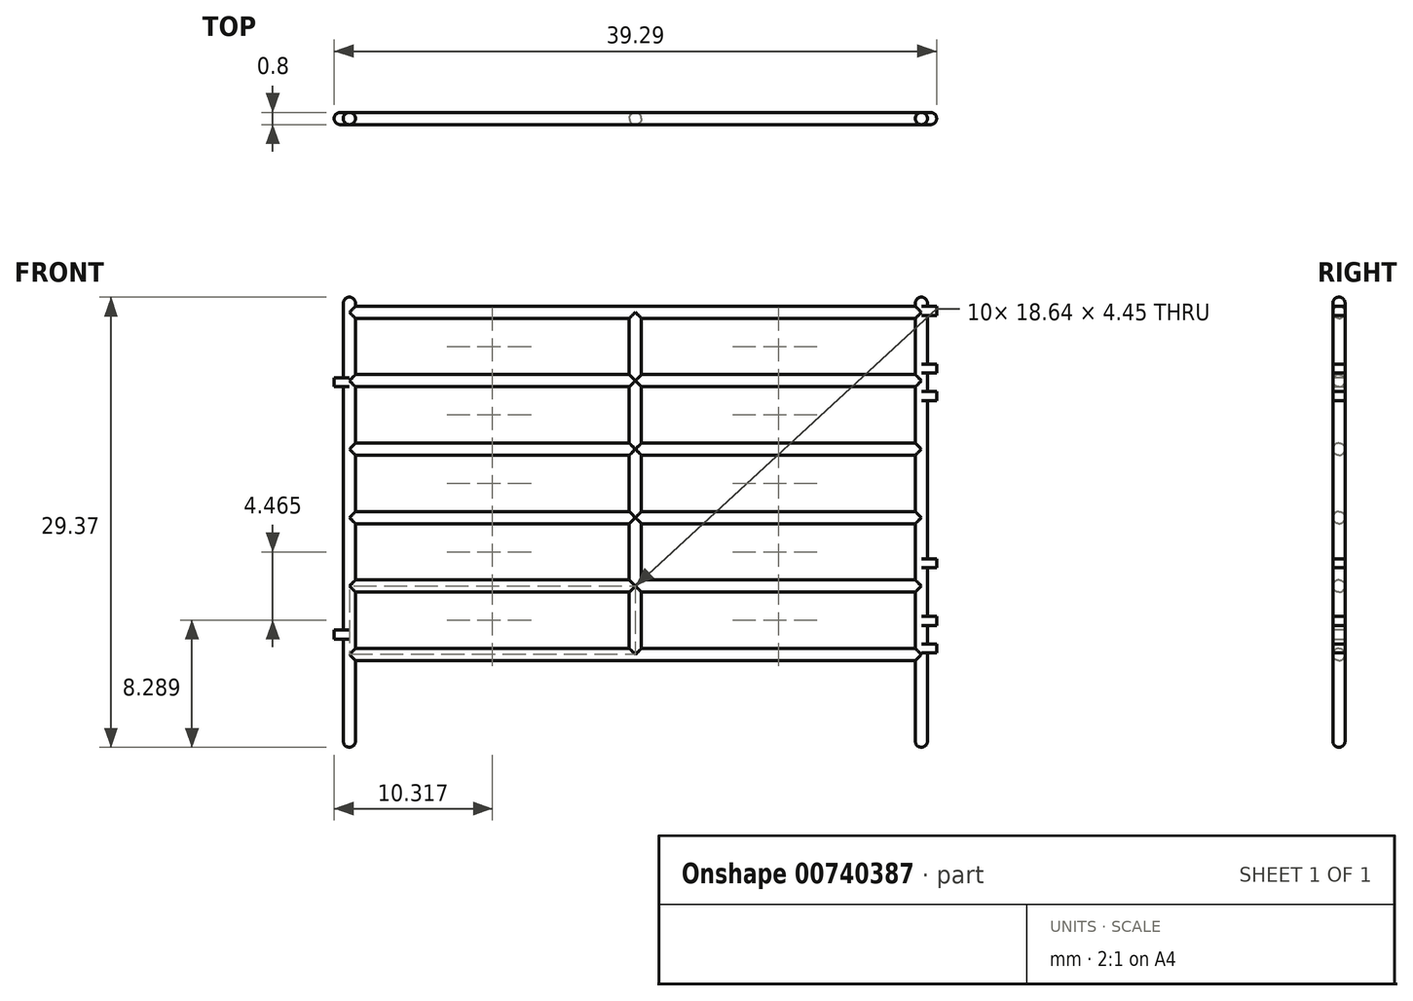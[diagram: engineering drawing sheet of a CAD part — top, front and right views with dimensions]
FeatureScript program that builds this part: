
annotation { "Feature Type Name" : "Feature", "Feature Type Description" : "" }
export const myFeature = defineFeature(function(context is Context, id is Id, definition is map)
    precondition{}
    {
        {
            var Q0;
            Q0=qCreatedBy(makeId("Front.planeOp"),FACE);
            var sketch = newSketch(context, id + "F0", { "sketchPlane" : qUnion([Q0])});
            skLineSegment(sketch, "E0", {"start": v(0, 0) * mm, "end": v(-36.51, 0) * mm});
            skLineSegment(sketch, "E1.0", {"start": v(0, 0.8) * mm, "end": v(-17.86, 0.8) * mm});
            skLineSegment(sketch, "E2.0", {"start": v(0, 4.46) * mm, "end": v(-17.86, 4.46) * mm});
            skLineSegment(sketch, "E3.0", {"start": v(0, 5.26) * mm, "end": v(-17.86, 5.26) * mm});
            skLineSegment(sketch, "E4.0", {"start": v(0, 8.93) * mm, "end": v(-17.86, 8.93) * mm});
            skLineSegment(sketch, "E5.0", {"start": v(0, 9.72) * mm, "end": v(-17.86, 9.72) * mm});
            skLineSegment(sketch, "E6.0", {"start": v(0, 13.4) * mm, "end": v(-17.86, 13.4) * mm});
            skLineSegment(sketch, "E7.0", {"start": v(0, 14.19) * mm, "end": v(-17.86, 14.19) * mm});
            skLineSegment(sketch, "E8.0", {"start": v(0, 17.86) * mm, "end": v(-17.86, 17.86) * mm});
            skLineSegment(sketch, "E9.0", {"start": v(0, 18.65) * mm, "end": v(-17.86, 18.65) * mm});
            skLineSegment(sketch, "E10.0", {"start": v(0, 22.32) * mm, "end": v(-17.86, 22.32) * mm});
            skLineSegment(sketch, "E11.0", {"start": v(0, 23.12) * mm, "end": v(-36.51, 23.12) * mm});
            skLineSegment(sketch, "E12", {"start": v(-36.51, 23.12) * mm, "end": v(-36.51, 23.32) * mm});
            skLineSegment(sketch, "E13", {"start": v(0, 23.12) * mm, "end": v(0, 23.32) * mm});
            skPoint(sketch, "E14", {"position": v(-37.3, 23.32) * mm});
            skLineSegment(sketch, "E15", {"start": v(-37.3, 23.32) * mm, "end": v(-37.3, 18.45) * mm});
            skLineSegment(sketch, "E16", {"start": v(-36.51, -5.26) * mm, "end": v(-36.51, 0) * mm});
            skLineSegment(sketch, "E17", {"start": v(-36.51, 0.8) * mm, "end": v(-36.51, 4.46) * mm});
            skLineSegment(sketch, "E18", {"start": v(-36.51, 5.26) * mm, "end": v(-36.51, 8.93) * mm});
            skLineSegment(sketch, "E19", {"start": v(-36.51, 9.72) * mm, "end": v(-36.51, 13.4) * mm});
            skLineSegment(sketch, "E20", {"start": v(-36.51, 14.19) * mm, "end": v(-36.51, 17.86) * mm});
            skLineSegment(sketch, "E21", {"start": v(-36.51, 18.65) * mm, "end": v(-36.51, 22.32) * mm});
            skLineSegment(sketch, "E22", {"start": v(0.8, 23.32) * mm, "end": v(0.8, 23.12) * mm});
            skLineSegment(sketch, "E23", {"start": v(0, -5.26) * mm, "end": v(0, 0) * mm});
            skLineSegment(sketch, "E24", {"start": v(0, 0.8) * mm, "end": v(0, 4.46) * mm});
            skLineSegment(sketch, "E25", {"start": v(0, 5.26) * mm, "end": v(0, 8.93) * mm});
            skLineSegment(sketch, "E26", {"start": v(0, 9.72) * mm, "end": v(0, 13.4) * mm});
            skLineSegment(sketch, "E27", {"start": v(0, 14.19) * mm, "end": v(0, 17.86) * mm});
            skLineSegment(sketch, "E28", {"start": v(0, 18.65) * mm, "end": v(0, 22.32) * mm});
            skArc(sketch, "E29", {"start": v(-37.3, -5.26) * mm, "mid": v(-36.9, -5.66) * mm, "end": v(-36.51, -5.26) * mm});
            skArc(sketch, "E30", {"start": v(0.8, -5.26) * mm, "mid": v(0.4, -5.66) * mm, "end": v(0, -5.26) * mm});
            skArc(sketch, "E31", {"start": v(0.8, 23.32) * mm, "mid": v(0.4, 23.71) * mm, "end": v(0, 23.32) * mm});
            skArc(sketch, "E32", {"start": v(-37.3, 23.32) * mm, "mid": v(-36.9, 23.71) * mm, "end": v(-36.51, 23.32) * mm});
            skPoint(sketch, "E33", {"position": v(0.8, 0.5) * mm});
            skLineSegment(sketch, "E34", {"start": v(0.8, 0.5) * mm, "end": v(1.39, 0.5) * mm});
            skLineSegment(sketch, "E35", {"start": v(1.39, 0.5) * mm, "end": v(1.39, 1.1) * mm});
            skLineSegment(sketch, "E36", {"start": v(1.39, 1.1) * mm, "end": v(0.8, 1.1) * mm});
            skLineSegment(sketch, "E37", {"start": v(0.8, 2.28) * mm, "end": v(1.39, 2.28) * mm});
            skLineSegment(sketch, "E38", {"start": v(1.39, 2.28) * mm, "end": v(1.39, 2.88) * mm});
            skLineSegment(sketch, "E39", {"start": v(1.39, 2.88) * mm, "end": v(0.8, 2.88) * mm});
            skLineSegment(sketch, "E40", {"start": v(0.8, 6.05) * mm, "end": v(1.39, 6.05) * mm});
            skLineSegment(sketch, "E41", {"start": v(1.39, 6.05) * mm, "end": v(1.39, 6.65) * mm});
            skLineSegment(sketch, "E42", {"start": v(1.39, 6.65) * mm, "end": v(0.8, 6.65) * mm});
            skLineSegment(sketch, "E43", {"start": v(0.8, 16.97) * mm, "end": v(1.39, 16.97) * mm});
            skLineSegment(sketch, "E44", {"start": v(1.39, 16.97) * mm, "end": v(1.39, 17.56) * mm});
            skLineSegment(sketch, "E45", {"start": v(1.39, 17.56) * mm, "end": v(0.8, 17.56) * mm});
            skLineSegment(sketch, "E46", {"start": v(0.8, 18.75) * mm, "end": v(1.39, 18.75) * mm});
            skLineSegment(sketch, "E47", {"start": v(1.39, 18.75) * mm, "end": v(1.39, 19.35) * mm});
            skLineSegment(sketch, "E48", {"start": v(1.39, 19.35) * mm, "end": v(0.8, 19.35) * mm});
            skLineSegment(sketch, "E49", {"start": v(0.8, 22.52) * mm, "end": v(1.39, 22.52) * mm});
            skLineSegment(sketch, "E50", {"start": v(1.39, 22.52) * mm, "end": v(1.39, 23.12) * mm});
            skLineSegment(sketch, "E51", {"start": v(1.39, 23.12) * mm, "end": v(0.8, 23.12) * mm});
            skPoint(sketch, "E52", {"position": v(-37.3, 1.39) * mm});
            skPoint(sketch, "E53", {"position": v(-37.9, 1.39) * mm});
            skLineSegment(sketch, "E54", {"start": v(-37.3, 1.39) * mm, "end": v(-37.9, 1.39) * mm});
            skLineSegment(sketch, "E55", {"start": v(-37.9, 1.39) * mm, "end": v(-37.9, 1.98) * mm});
            skLineSegment(sketch, "E56", {"start": v(-37.9, 1.98) * mm, "end": v(-37.3, 1.98) * mm});
            skPoint(sketch, "E57", {"position": v(-37.3, 17.86) * mm});
            skLineSegment(sketch, "E58", {"start": v(-37.3, 17.86) * mm, "end": v(-37.9, 17.86) * mm});
            skLineSegment(sketch, "E59", {"start": v(-37.9, 17.86) * mm, "end": v(-37.9, 18.45) * mm});
            skLineSegment(sketch, "E60", {"start": v(-37.9, 18.45) * mm, "end": v(-37.3, 18.45) * mm});
            skLineSegment(sketch, "E61.trimOffspring", {"start": v(-37.3, 17.86) * mm, "end": v(-37.3, 1.98) * mm});
            skLineSegment(sketch, "E62.trimOffspring", {"start": v(-37.3, 1.39) * mm, "end": v(-37.3, -5.26) * mm});
            skLineSegment(sketch, "E63.trimOffspring", {"start": v(0.8, 0.5) * mm, "end": v(0.8, -5.26) * mm});
            skLineSegment(sketch, "E64.trimOffspring", {"start": v(0.8, 2.28) * mm, "end": v(0.8, 1.1) * mm});
            skLineSegment(sketch, "E65.trimOffspring", {"start": v(0.8, 6.05) * mm, "end": v(0.8, 2.88) * mm});
            skLineSegment(sketch, "E66.trimOffspring", {"start": v(0.8, 16.97) * mm, "end": v(0.8, 6.65) * mm});
            skLineSegment(sketch, "E67.trimOffspring", {"start": v(0.8, 18.75) * mm, "end": v(0.8, 17.56) * mm});
            skLineSegment(sketch, "E68.trimOffspring", {"start": v(0.8, 22.52) * mm, "end": v(0.8, 19.35) * mm});
            skLineSegment(sketch, "E69", {"start": v(-18.65, 0.8) * mm, "end": v(-18.65, 4.46) * mm});
            skLineSegment(sketch, "E70.0", {"start": v(-17.86, 0.8) * mm, "end": v(-17.86, 4.46) * mm});
            skLineSegment(sketch, "E71", {"start": v(-18.65, 5.26) * mm, "end": v(-18.65, 8.93) * mm});
            skLineSegment(sketch, "E72", {"start": v(-17.86, 5.26) * mm, "end": v(-17.86, 8.93) * mm});
            skLineSegment(sketch, "E73", {"start": v(-18.65, 9.72) * mm, "end": v(-18.65, 13.4) * mm});
            skLineSegment(sketch, "E74", {"start": v(-17.86, 9.72) * mm, "end": v(-17.86, 13.4) * mm});
            skPoint(sketch, "E74.endSnap0", {"position": v(-18.26, 13.4) * mm});
            skLineSegment(sketch, "E75", {"start": v(-18.65, 14.19) * mm, "end": v(-18.65, 17.86) * mm});
            skLineSegment(sketch, "E76", {"start": v(-17.86, 14.19) * mm, "end": v(-17.86, 17.86) * mm});
            skLineSegment(sketch, "E77", {"start": v(-18.65, 18.65) * mm, "end": v(-18.65, 22.32) * mm});
            skLineSegment(sketch, "E78", {"start": v(-17.86, 18.65) * mm, "end": v(-17.86, 22.32) * mm});
            skLineSegment(sketch, "E79.trimOffspring", {"start": v(-18.65, 22.32) * mm, "end": v(-36.51, 22.32) * mm});
            skLineSegment(sketch, "E80.trimOffspring", {"start": v(-18.65, 18.65) * mm, "end": v(-36.51, 18.65) * mm});
            skLineSegment(sketch, "E81.trimOffspring", {"start": v(-18.65, 17.86) * mm, "end": v(-36.51, 17.86) * mm});
            skLineSegment(sketch, "E82.trimOffspring", {"start": v(-18.65, 14.19) * mm, "end": v(-36.51, 14.19) * mm});
            skLineSegment(sketch, "E83.trimOffspring", {"start": v(-18.65, 13.4) * mm, "end": v(-36.51, 13.4) * mm});
            skLineSegment(sketch, "E84.trimOffspring", {"start": v(-18.65, 9.72) * mm, "end": v(-36.51, 9.72) * mm});
            skLineSegment(sketch, "E85.trimOffspring", {"start": v(-18.65, 8.93) * mm, "end": v(-36.51, 8.93) * mm});
            skLineSegment(sketch, "E86.trimOffspring", {"start": v(-18.65, 5.26) * mm, "end": v(-36.51, 5.26) * mm});
            skLineSegment(sketch, "E87.trimOffspring", {"start": v(-18.65, 4.46) * mm, "end": v(-36.51, 4.46) * mm});
            skLineSegment(sketch, "E88.trimOffspring", {"start": v(-18.65, 0.8) * mm, "end": v(-36.51, 0.8) * mm});
            skSolve(sketch);
        }
        {
            var Q0;
            Q0=makeQuery(id+"F0.imprint","IMPRINT",FACE,{"disambiguationData":[TD([[makeQuery(id+"F0.imprint","IMPRINT",EDGE,{"derivedFrom":sQuery(id+"F0.wireOp",EDGE,"E0")}),-1.0]])]});
            extrude(context, id + "F1", {"entities" : qUnion([Q0]), "endBound" : BoundingType.SYMMETRIC, "depth" : 0.8 * mm, "offsetDistance" : 25.4 * mm});
        }
        {
            var Q0;
            Q0=makeQuery(id+"F1.opExtrude","CAP_EDGE",EDGE,{"disambiguationData":[OSD([sQuery(id+"F0.wireOp",EDGE,"E79.trimOffspring")])],"isStart":false});
            var Q1;
            Q1=makeQuery(id+"F1.opExtrude","CAP_EDGE",EDGE,{"disambiguationData":[OSD([sQuery(id+"F0.wireOp",EDGE,"E11.0")])],"isStart":false});
            var Q2;
            Q2=makeQuery(id+"F1.opExtrude","CAP_EDGE",EDGE,{"disambiguationData":[OSD([sQuery(id+"F0.wireOp",EDGE,"E32")])],"isStart":false});
            var Q3;
            Q3=makeQuery(id+"F1.opExtrude","CAP_EDGE",EDGE,{"disambiguationData":[OSD([sQuery(id+"F0.wireOp",EDGE,"E12")])],"isStart":false});
            var Q4;
            Q4=makeQuery(id+"F1.opExtrude","CAP_EDGE",EDGE,{"disambiguationData":[OSD([sQuery(id+"F0.wireOp",EDGE,"E15")])],"isStart":false});
            var Q5;
            Q5=makeQuery(id+"F1.opExtrude","CAP_EDGE",EDGE,{"disambiguationData":[OSD([sQuery(id+"F0.wireOp",EDGE,"E21")])],"isStart":false});
            var Q6;
            Q6=makeQuery(id+"F1.opExtrude","CAP_EDGE",EDGE,{"disambiguationData":[OSD([sQuery(id+"F0.wireOp",EDGE,"E77")])],"isStart":false});
            var Q7;
            Q7=makeQuery(id+"F1.opExtrude","CAP_EDGE",EDGE,{"disambiguationData":[OSD([sQuery(id+"F0.wireOp",EDGE,"E78")])],"isStart":false});
            var Q8;
            Q8=makeQuery(id+"F1.opExtrude","CAP_EDGE",EDGE,{"disambiguationData":[OSD([sQuery(id+"F0.wireOp",EDGE,"E10.0")])],"isStart":false});
            var Q9;
            Q9=makeQuery(id+"F1.opExtrude","CAP_EDGE",EDGE,{"disambiguationData":[OSD([sQuery(id+"F0.wireOp",EDGE,"E9.0")])],"isStart":false});
            var Q10;
            Q10=makeQuery(id+"F1.opExtrude","CAP_EDGE",EDGE,{"disambiguationData":[OSD([sQuery(id+"F0.wireOp",EDGE,"E80.trimOffspring")])],"isStart":false});
            var Q11;
            Q11=makeQuery(id+"F1.opExtrude","CAP_EDGE",EDGE,{"disambiguationData":[OSD([sQuery(id+"F0.wireOp",EDGE,"E81.trimOffspring")])],"isStart":false});
            var Q12;
            Q12=makeQuery(id+"F1.opExtrude","CAP_EDGE",EDGE,{"disambiguationData":[OSD([sQuery(id+"F0.wireOp",EDGE,"E8.0")])],"isStart":false});
            var Q13;
            Q13=makeQuery(id+"F1.opExtrude","CAP_EDGE",EDGE,{"disambiguationData":[OSD([sQuery(id+"F0.wireOp",EDGE,"E75")])],"isStart":false});
            var Q14;
            Q14=makeQuery(id+"F1.opExtrude","CAP_EDGE",EDGE,{"disambiguationData":[OSD([sQuery(id+"F0.wireOp",EDGE,"E76")])],"isStart":false});
            var Q15;
            Q15=makeQuery(id+"F1.opExtrude","CAP_EDGE",EDGE,{"disambiguationData":[OSD([sQuery(id+"F0.wireOp",EDGE,"E82.trimOffspring")])],"isStart":false});
            var Q16;
            Q16=makeQuery(id+"F1.opExtrude","CAP_EDGE",EDGE,{"disambiguationData":[OSD([sQuery(id+"F0.wireOp",EDGE,"E20")])],"isStart":false});
            var Q17;
            Q17=makeQuery(id+"F1.opExtrude","CAP_EDGE",EDGE,{"disambiguationData":[OSD([sQuery(id+"F0.wireOp",EDGE,"E61.trimOffspring")])],"isStart":false});
            var Q18;
            Q18=makeQuery(id+"F1.opExtrude","CAP_EDGE",EDGE,{"disambiguationData":[OSD([sQuery(id+"F0.wireOp",EDGE,"E83.trimOffspring")])],"isStart":false});
            var Q19;
            Q19=makeQuery(id+"F1.opExtrude","CAP_EDGE",EDGE,{"disambiguationData":[OSD([sQuery(id+"F0.wireOp",EDGE,"E7.0")])],"isStart":false});
            var Q20;
            Q20=makeQuery(id+"F1.opExtrude","CAP_EDGE",EDGE,{"disambiguationData":[OSD([sQuery(id+"F0.wireOp",EDGE,"E6.0")])],"isStart":false});
            var Q21;
            Q21=makeQuery(id+"F1.opExtrude","CAP_EDGE",EDGE,{"disambiguationData":[OSD([sQuery(id+"F0.wireOp",EDGE,"E74")])],"isStart":false});
            var Q22;
            Q22=makeQuery(id+"F1.opExtrude","CAP_EDGE",EDGE,{"disambiguationData":[OSD([sQuery(id+"F0.wireOp",EDGE,"E73")])],"isStart":false});
            var Q23;
            Q23=makeQuery(id+"F1.opExtrude","CAP_EDGE",EDGE,{"disambiguationData":[OSD([sQuery(id+"F0.wireOp",EDGE,"E19")])],"isStart":false});
            var Q24;
            Q24=makeQuery(id+"F1.opExtrude","CAP_EDGE",EDGE,{"disambiguationData":[OSD([sQuery(id+"F0.wireOp",EDGE,"E84.trimOffspring")])],"isStart":false});
            var Q25;
            Q25=makeQuery(id+"F1.opExtrude","CAP_EDGE",EDGE,{"disambiguationData":[OSD([sQuery(id+"F0.wireOp",EDGE,"E5.0")])],"isStart":false});
            var Q26;
            Q26=makeQuery(id+"F1.opExtrude","CAP_EDGE",EDGE,{"disambiguationData":[OSD([sQuery(id+"F0.wireOp",EDGE,"E4.0")])],"isStart":false});
            var Q27;
            Q27=makeQuery(id+"F1.opExtrude","CAP_EDGE",EDGE,{"disambiguationData":[OSD([sQuery(id+"F0.wireOp",EDGE,"E72")])],"isStart":false});
            var Q28;
            Q28=makeQuery(id+"F1.opExtrude","CAP_EDGE",EDGE,{"disambiguationData":[OSD([sQuery(id+"F0.wireOp",EDGE,"E71")])],"isStart":false});
            var Q29;
            Q29=makeQuery(id+"F1.opExtrude","CAP_EDGE",EDGE,{"disambiguationData":[OSD([sQuery(id+"F0.wireOp",EDGE,"E85.trimOffspring")])],"isStart":false});
            var Q30;
            Q30=makeQuery(id+"F1.opExtrude","CAP_EDGE",EDGE,{"disambiguationData":[OSD([sQuery(id+"F0.wireOp",EDGE,"E18")])],"isStart":false});
            var Q31;
            Q31=makeQuery(id+"F1.opExtrude","CAP_EDGE",EDGE,{"disambiguationData":[OSD([sQuery(id+"F0.wireOp",EDGE,"E86.trimOffspring")])],"isStart":false});
            var Q32;
            Q32=makeQuery(id+"F1.opExtrude","CAP_EDGE",EDGE,{"disambiguationData":[OSD([sQuery(id+"F0.wireOp",EDGE,"E3.0")])],"isStart":false});
            var Q33;
            Q33=makeQuery(id+"F1.opExtrude","CAP_EDGE",EDGE,{"disambiguationData":[OSD([sQuery(id+"F0.wireOp",EDGE,"E2.0")])],"isStart":false});
            var Q34;
            Q34=makeQuery(id+"F1.opExtrude","CAP_EDGE",EDGE,{"disambiguationData":[OSD([sQuery(id+"F0.wireOp",EDGE,"E87.trimOffspring")])],"isStart":false});
            var Q35;
            Q35=makeQuery(id+"F1.opExtrude","CAP_EDGE",EDGE,{"disambiguationData":[OSD([sQuery(id+"F0.wireOp",EDGE,"E69")])],"isStart":false});
            var Q36;
            Q36=makeQuery(id+"F1.opExtrude","CAP_EDGE",EDGE,{"disambiguationData":[OSD([sQuery(id+"F0.wireOp",EDGE,"E70.0")])],"isStart":false});
            var Q37;
            Q37=makeQuery(id+"F1.opExtrude","CAP_EDGE",EDGE,{"disambiguationData":[OSD([sQuery(id+"F0.wireOp",EDGE,"E17")])],"isStart":false});
            var Q38;
            Q38=makeQuery(id+"F1.opExtrude","CAP_EDGE",EDGE,{"disambiguationData":[OSD([sQuery(id+"F0.wireOp",EDGE,"E88.trimOffspring")])],"isStart":false});
            var Q39;
            Q39=makeQuery(id+"F1.opExtrude","CAP_EDGE",EDGE,{"disambiguationData":[OSD([sQuery(id+"F0.wireOp",EDGE,"E62.trimOffspring")])],"isStart":false});
            var Q40;
            Q40=makeQuery(id+"F1.opExtrude","CAP_EDGE",EDGE,{"disambiguationData":[OSD([sQuery(id+"F0.wireOp",EDGE,"E1.0")])],"isStart":false});
            var Q41;
            Q41=makeQuery(id+"F1.opExtrude","CAP_EDGE",EDGE,{"disambiguationData":[OSD([sQuery(id+"F0.wireOp",EDGE,"E0")])],"isStart":false});
            var Q42;
            Q42=makeQuery(id+"F1.opExtrude","CAP_EDGE",EDGE,{"disambiguationData":[OSD([sQuery(id+"F0.wireOp",EDGE,"E16")])],"isStart":false});
            var Q43;
            Q43=makeQuery(id+"F1.opExtrude","CAP_EDGE",EDGE,{"disambiguationData":[OSD([sQuery(id+"F0.wireOp",EDGE,"E29")])],"isStart":false});
            var Q44;
            Q44=makeQuery(id+"F1.opExtrude","CAP_EDGE",EDGE,{"disambiguationData":[OSD([sQuery(id+"F0.wireOp",EDGE,"E23")])],"isStart":false});
            var Q45;
            Q45=makeQuery(id+"F1.opExtrude","CAP_EDGE",EDGE,{"disambiguationData":[OSD([sQuery(id+"F0.wireOp",EDGE,"E30")])],"isStart":false});
            var Q46;
            Q46=makeQuery(id+"F1.opExtrude","CAP_EDGE",EDGE,{"disambiguationData":[OSD([sQuery(id+"F0.wireOp",EDGE,"E63.trimOffspring")])],"isStart":false});
            var Q47;
            Q47=makeQuery(id+"F1.opExtrude","CAP_EDGE",EDGE,{"disambiguationData":[OSD([sQuery(id+"F0.wireOp",EDGE,"E64.trimOffspring")])],"isStart":false});
            var Q48;
            Q48=makeQuery(id+"F1.opExtrude","CAP_EDGE",EDGE,{"disambiguationData":[OSD([sQuery(id+"F0.wireOp",EDGE,"E24")])],"isStart":false});
            var Q49;
            Q49=makeQuery(id+"F1.opExtrude","CAP_EDGE",EDGE,{"disambiguationData":[OSD([sQuery(id+"F0.wireOp",EDGE,"E65.trimOffspring")])],"isStart":false});
            var Q50;
            Q50=makeQuery(id+"F1.opExtrude","CAP_EDGE",EDGE,{"disambiguationData":[OSD([sQuery(id+"F0.wireOp",EDGE,"E25")])],"isStart":false});
            var Q51;
            Q51=makeQuery(id+"F1.opExtrude","CAP_EDGE",EDGE,{"disambiguationData":[OSD([sQuery(id+"F0.wireOp",EDGE,"E66.trimOffspring")])],"isStart":false});
            var Q52;
            Q52=makeQuery(id+"F1.opExtrude","CAP_EDGE",EDGE,{"disambiguationData":[OSD([sQuery(id+"F0.wireOp",EDGE,"E26")])],"isStart":false});
            var Q53;
            Q53=makeQuery(id+"F1.opExtrude","CAP_EDGE",EDGE,{"disambiguationData":[OSD([sQuery(id+"F0.wireOp",EDGE,"E27")])],"isStart":false});
            var Q54;
            Q54=makeQuery(id+"F1.opExtrude","CAP_EDGE",EDGE,{"disambiguationData":[OSD([sQuery(id+"F0.wireOp",EDGE,"E67.trimOffspring")])],"isStart":false});
            var Q55;
            Q55=makeQuery(id+"F1.opExtrude","CAP_EDGE",EDGE,{"disambiguationData":[OSD([sQuery(id+"F0.wireOp",EDGE,"E28")])],"isStart":false});
            var Q56;
            Q56=makeQuery(id+"F1.opExtrude","CAP_EDGE",EDGE,{"disambiguationData":[OSD([sQuery(id+"F0.wireOp",EDGE,"E68.trimOffspring")])],"isStart":false});
            var Q57;
            Q57=makeQuery(id+"F1.opExtrude","CAP_EDGE",EDGE,{"disambiguationData":[OSD([sQuery(id+"F0.wireOp",EDGE,"E31")])],"isStart":false});
            var Q58;
            Q58=makeQuery(id+"F1.opExtrude","CAP_EDGE",EDGE,{"disambiguationData":[OSD([sQuery(id+"F0.wireOp",EDGE,"E22")])],"isStart":false});
            var Q59;
            Q59=makeQuery(id+"F1.opExtrude","CAP_EDGE",EDGE,{"disambiguationData":[OSD([sQuery(id+"F0.wireOp",EDGE,"E13")])],"isStart":false});
            var Q60;
            Q60=makeQuery(id+"F1.opExtrude","CAP_EDGE",EDGE,{"disambiguationData":[OSD([sQuery(id+"F0.wireOp",EDGE,"E11.0")])],"isStart":true});
            var Q61;
            Q61=makeQuery(id+"F1.opExtrude","CAP_EDGE",EDGE,{"disambiguationData":[OSD([sQuery(id+"F0.wireOp",EDGE,"E31")])],"isStart":true});
            var Q62;
            Q62=makeQuery(id+"F1.opExtrude","CAP_EDGE",EDGE,{"disambiguationData":[OSD([sQuery(id+"F0.wireOp",EDGE,"E22")])],"isStart":true});
            var Q63;
            Q63=makeQuery(id+"F1.opExtrude","CAP_EDGE",EDGE,{"disambiguationData":[OSD([sQuery(id+"F0.wireOp",EDGE,"E13")])],"isStart":true});
            var Q64;
            Q64=makeQuery(id+"F1.opExtrude","CAP_EDGE",EDGE,{"disambiguationData":[OSD([sQuery(id+"F0.wireOp",EDGE,"E10.0")])],"isStart":true});
            var Q65;
            Q65=makeQuery(id+"F1.opExtrude","CAP_EDGE",EDGE,{"disambiguationData":[OSD([sQuery(id+"F0.wireOp",EDGE,"E9.0")])],"isStart":true});
            var Q66;
            Q66=makeQuery(id+"F1.opExtrude","CAP_EDGE",EDGE,{"disambiguationData":[OSD([sQuery(id+"F0.wireOp",EDGE,"E8.0")])],"isStart":true});
            var Q67;
            Q67=makeQuery(id+"F1.opExtrude","CAP_EDGE",EDGE,{"disambiguationData":[OSD([sQuery(id+"F0.wireOp",EDGE,"E28")])],"isStart":true});
            var Q68;
            Q68=makeQuery(id+"F1.opExtrude","CAP_EDGE",EDGE,{"disambiguationData":[OSD([sQuery(id+"F0.wireOp",EDGE,"E68.trimOffspring")])],"isStart":true});
            var Q69;
            Q69=makeQuery(id+"F1.opExtrude","CAP_EDGE",EDGE,{"disambiguationData":[OSD([sQuery(id+"F0.wireOp",EDGE,"E50")])],"isStart":true});
            var Q70;
            Q70=makeQuery(id+"F1.opExtrude","CAP_EDGE",EDGE,{"disambiguationData":[OSD([sQuery(id+"F0.wireOp",EDGE,"E50")])],"isStart":false});
            var Q71;
            Q71=makeQuery(id+"F1.opExtrude","CAP_EDGE",EDGE,{"disambiguationData":[OSD([sQuery(id+"F0.wireOp",EDGE,"E47")])],"isStart":true});
            var Q72;
            Q72=makeQuery(id+"F1.opExtrude","CAP_EDGE",EDGE,{"disambiguationData":[OSD([sQuery(id+"F0.wireOp",EDGE,"E47")])],"isStart":false});
            var Q73;
            Q73=makeQuery(id+"F1.opExtrude","CAP_EDGE",EDGE,{"disambiguationData":[OSD([sQuery(id+"F0.wireOp",EDGE,"E67.trimOffspring")])],"isStart":true});
            var Q74;
            Q74=makeQuery(id+"F1.opExtrude","CAP_EDGE",EDGE,{"disambiguationData":[OSD([sQuery(id+"F0.wireOp",EDGE,"E27")])],"isStart":true});
            var Q75;
            Q75=makeQuery(id+"F1.opExtrude","CAP_EDGE",EDGE,{"disambiguationData":[OSD([sQuery(id+"F0.wireOp",EDGE,"E66.trimOffspring")])],"isStart":true});
            var Q76;
            Q76=makeQuery(id+"F1.opExtrude","CAP_EDGE",EDGE,{"disambiguationData":[OSD([sQuery(id+"F0.wireOp",EDGE,"E7.0")])],"isStart":true});
            var Q77;
            Q77=makeQuery(id+"F1.opExtrude","CAP_EDGE",EDGE,{"disambiguationData":[OSD([sQuery(id+"F0.wireOp",EDGE,"E76")])],"isStart":true});
            var Q78;
            Q78=makeQuery(id+"F1.opExtrude","CAP_EDGE",EDGE,{"disambiguationData":[OSD([sQuery(id+"F0.wireOp",EDGE,"E74")])],"isStart":true});
            var Q79;
            Q79=makeQuery(id+"F1.opExtrude","CAP_EDGE",EDGE,{"disambiguationData":[OSD([sQuery(id+"F0.wireOp",EDGE,"E72")])],"isStart":true});
            var Q80;
            Q80=makeQuery(id+"F1.opExtrude","CAP_EDGE",EDGE,{"disambiguationData":[OSD([sQuery(id+"F0.wireOp",EDGE,"E4.0")])],"isStart":true});
            var Q81;
            Q81=makeQuery(id+"F1.opExtrude","CAP_EDGE",EDGE,{"disambiguationData":[OSD([sQuery(id+"F0.wireOp",EDGE,"E5.0")])],"isStart":true});
            var Q82;
            Q82=makeQuery(id+"F1.opExtrude","CAP_EDGE",EDGE,{"disambiguationData":[OSD([sQuery(id+"F0.wireOp",EDGE,"E26")])],"isStart":true});
            var Q83;
            Q83=makeQuery(id+"F1.opExtrude","CAP_EDGE",EDGE,{"disambiguationData":[OSD([sQuery(id+"F0.wireOp",EDGE,"E25")])],"isStart":true});
            var Q84;
            Q84=makeQuery(id+"F1.opExtrude","CAP_EDGE",EDGE,{"disambiguationData":[OSD([sQuery(id+"F0.wireOp",EDGE,"E41")])],"isStart":true});
            var Q85;
            Q85=makeQuery(id+"F1.opExtrude","CAP_EDGE",EDGE,{"disambiguationData":[OSD([sQuery(id+"F0.wireOp",EDGE,"E41")])],"isStart":false});
            var Q86;
            Q86=makeQuery(id+"F1.opExtrude","CAP_EDGE",EDGE,{"disambiguationData":[OSD([sQuery(id+"F0.wireOp",EDGE,"E2.0")])],"isStart":true});
            var Q87;
            Q87=makeQuery(id+"F1.opExtrude","CAP_EDGE",EDGE,{"disambiguationData":[OSD([sQuery(id+"F0.wireOp",EDGE,"E65.trimOffspring")])],"isStart":true});
            var Q88;
            Q88=makeQuery(id+"F1.opExtrude","CAP_EDGE",EDGE,{"disambiguationData":[OSD([sQuery(id+"F0.wireOp",EDGE,"E24")])],"isStart":true});
            var Q89;
            Q89=makeQuery(id+"F1.opExtrude","CAP_EDGE",EDGE,{"disambiguationData":[OSD([sQuery(id+"F0.wireOp",EDGE,"E1.0")])],"isStart":true});
            var Q90;
            Q90=makeQuery(id+"F1.opExtrude","CAP_EDGE",EDGE,{"disambiguationData":[OSD([sQuery(id+"F0.wireOp",EDGE,"E0")])],"isStart":true});
            var Q91;
            Q91=makeQuery(id+"F1.opExtrude","CAP_EDGE",EDGE,{"disambiguationData":[OSD([sQuery(id+"F0.wireOp",EDGE,"E64.trimOffspring")])],"isStart":true});
            var Q92;
            Q92=makeQuery(id+"F1.opExtrude","CAP_EDGE",EDGE,{"disambiguationData":[OSD([sQuery(id+"F0.wireOp",EDGE,"E63.trimOffspring")])],"isStart":true});
            var Q93;
            Q93=makeQuery(id+"F1.opExtrude","CAP_EDGE",EDGE,{"disambiguationData":[OSD([sQuery(id+"F0.wireOp",EDGE,"E23")])],"isStart":true});
            var Q94;
            Q94=makeQuery(id+"F1.opExtrude","CAP_EDGE",EDGE,{"disambiguationData":[OSD([sQuery(id+"F0.wireOp",EDGE,"E30")])],"isStart":true});
            var Q95;
            Q95=makeQuery(id+"F1.opExtrude","CAP_EDGE",EDGE,{"disambiguationData":[OSD([sQuery(id+"F0.wireOp",EDGE,"E38")])],"isStart":false});
            var Q96;
            Q96=makeQuery(id+"F1.opExtrude","CAP_EDGE",EDGE,{"disambiguationData":[OSD([sQuery(id+"F0.wireOp",EDGE,"E38")])],"isStart":true});
            var Q97;
            Q97=makeQuery(id+"F1.opExtrude","CAP_EDGE",EDGE,{"disambiguationData":[OSD([sQuery(id+"F0.wireOp",EDGE,"E35")])],"isStart":false});
            var Q98;
            Q98=makeQuery(id+"F1.opExtrude","CAP_EDGE",EDGE,{"disambiguationData":[OSD([sQuery(id+"F0.wireOp",EDGE,"E35")])],"isStart":true});
            var Q99;
            Q99=makeQuery(id+"F1.opExtrude","CAP_EDGE",EDGE,{"disambiguationData":[OSD([sQuery(id+"F0.wireOp",EDGE,"E44")])],"isStart":true});
            var Q100;
            Q100=makeQuery(id+"F1.opExtrude","CAP_EDGE",EDGE,{"disambiguationData":[OSD([sQuery(id+"F0.wireOp",EDGE,"E44")])],"isStart":false});
            var Q101;
            Q101=makeQuery(id+"F1.opExtrude","CAP_EDGE",EDGE,{"disambiguationData":[OSD([sQuery(id+"F0.wireOp",EDGE,"E78")])],"isStart":true});
            var Q102;
            Q102=makeQuery(id+"F1.opExtrude","CAP_EDGE",EDGE,{"disambiguationData":[OSD([sQuery(id+"F0.wireOp",EDGE,"E77")])],"isStart":true});
            var Q103;
            Q103=makeQuery(id+"F1.opExtrude","CAP_EDGE",EDGE,{"disambiguationData":[OSD([sQuery(id+"F0.wireOp",EDGE,"E79.trimOffspring")])],"isStart":true});
            var Q104;
            Q104=makeQuery(id+"F1.opExtrude","CAP_EDGE",EDGE,{"disambiguationData":[OSD([sQuery(id+"F0.wireOp",EDGE,"E80.trimOffspring")])],"isStart":true});
            var Q105;
            Q105=makeQuery(id+"F1.opExtrude","CAP_EDGE",EDGE,{"disambiguationData":[OSD([sQuery(id+"F0.wireOp",EDGE,"E81.trimOffspring")])],"isStart":true});
            var Q106;
            Q106=makeQuery(id+"F1.opExtrude","CAP_EDGE",EDGE,{"disambiguationData":[OSD([sQuery(id+"F0.wireOp",EDGE,"E75")])],"isStart":true});
            var Q107;
            Q107=makeQuery(id+"F1.opExtrude","CAP_EDGE",EDGE,{"disambiguationData":[OSD([sQuery(id+"F0.wireOp",EDGE,"E82.trimOffspring")])],"isStart":true});
            var Q108;
            Q108=makeQuery(id+"F1.opExtrude","CAP_EDGE",EDGE,{"disambiguationData":[OSD([sQuery(id+"F0.wireOp",EDGE,"E83.trimOffspring")])],"isStart":true});
            var Q109;
            Q109=makeQuery(id+"F1.opExtrude","CAP_EDGE",EDGE,{"disambiguationData":[OSD([sQuery(id+"F0.wireOp",EDGE,"E73")])],"isStart":true});
            var Q110;
            Q110=makeQuery(id+"F1.opExtrude","CAP_EDGE",EDGE,{"disambiguationData":[OSD([sQuery(id+"F0.wireOp",EDGE,"E84.trimOffspring")])],"isStart":true});
            var Q111;
            Q111=makeQuery(id+"F1.opExtrude","CAP_EDGE",EDGE,{"disambiguationData":[OSD([sQuery(id+"F0.wireOp",EDGE,"E85.trimOffspring")])],"isStart":true});
            var Q112;
            Q112=makeQuery(id+"F1.opExtrude","CAP_EDGE",EDGE,{"disambiguationData":[OSD([sQuery(id+"F0.wireOp",EDGE,"E71")])],"isStart":true});
            var Q113;
            Q113=makeQuery(id+"F1.opExtrude","CAP_EDGE",EDGE,{"disambiguationData":[OSD([sQuery(id+"F0.wireOp",EDGE,"E6.0")])],"isStart":true});
            var Q114;
            Q114=makeQuery(id+"F1.opExtrude","CAP_EDGE",EDGE,{"disambiguationData":[OSD([sQuery(id+"F0.wireOp",EDGE,"E86.trimOffspring")])],"isStart":true});
            var Q115;
            Q115=makeQuery(id+"F1.opExtrude","CAP_EDGE",EDGE,{"disambiguationData":[OSD([sQuery(id+"F0.wireOp",EDGE,"E87.trimOffspring")])],"isStart":true});
            var Q116;
            Q116=makeQuery(id+"F1.opExtrude","CAP_EDGE",EDGE,{"disambiguationData":[OSD([sQuery(id+"F0.wireOp",EDGE,"E70.0")])],"isStart":true});
            var Q117;
            Q117=makeQuery(id+"F1.opExtrude","CAP_EDGE",EDGE,{"disambiguationData":[OSD([sQuery(id+"F0.wireOp",EDGE,"E69")])],"isStart":true});
            var Q118;
            Q118=makeQuery(id+"F1.opExtrude","CAP_EDGE",EDGE,{"disambiguationData":[OSD([sQuery(id+"F0.wireOp",EDGE,"E16")])],"isStart":true});
            var Q119;
            Q119=makeQuery(id+"F1.opExtrude","CAP_EDGE",EDGE,{"disambiguationData":[OSD([sQuery(id+"F0.wireOp",EDGE,"E29")])],"isStart":true});
            var Q120;
            Q120=makeQuery(id+"F1.opExtrude","CAP_EDGE",EDGE,{"disambiguationData":[OSD([sQuery(id+"F0.wireOp",EDGE,"E62.trimOffspring")])],"isStart":true});
            var Q121;
            Q121=makeQuery(id+"F1.opExtrude","CAP_EDGE",EDGE,{"disambiguationData":[OSD([sQuery(id+"F0.wireOp",EDGE,"E17")])],"isStart":true});
            var Q122;
            Q122=makeQuery(id+"F1.opExtrude","CAP_EDGE",EDGE,{"disambiguationData":[OSD([sQuery(id+"F0.wireOp",EDGE,"E61.trimOffspring")])],"isStart":true});
            var Q123;
            Q123=makeQuery(id+"F1.opExtrude","CAP_EDGE",EDGE,{"disambiguationData":[OSD([sQuery(id+"F0.wireOp",EDGE,"E18")])],"isStart":true});
            var Q124;
            Q124=makeQuery(id+"F1.opExtrude","CAP_EDGE",EDGE,{"disambiguationData":[OSD([sQuery(id+"F0.wireOp",EDGE,"E20")])],"isStart":true});
            var Q125;
            Q125=makeQuery(id+"F1.opExtrude","CAP_EDGE",EDGE,{"disambiguationData":[OSD([sQuery(id+"F0.wireOp",EDGE,"E21")])],"isStart":true});
            var Q126;
            Q126=makeQuery(id+"F1.opExtrude","CAP_EDGE",EDGE,{"disambiguationData":[OSD([sQuery(id+"F0.wireOp",EDGE,"E12")])],"isStart":true});
            var Q127;
            Q127=makeQuery(id+"F1.opExtrude","CAP_EDGE",EDGE,{"disambiguationData":[OSD([sQuery(id+"F0.wireOp",EDGE,"E32")])],"isStart":true});
            var Q128;
            Q128=makeQuery(id+"F1.opExtrude","CAP_EDGE",EDGE,{"disambiguationData":[OSD([sQuery(id+"F0.wireOp",EDGE,"E15")])],"isStart":true});
            var Q129;
            Q129=makeQuery(id+"F1.opExtrude","CAP_EDGE",EDGE,{"disambiguationData":[OSD([sQuery(id+"F0.wireOp",EDGE,"E59")])],"isStart":true});
            var Q130;
            Q130=makeQuery(id+"F1.opExtrude","CAP_EDGE",EDGE,{"disambiguationData":[OSD([sQuery(id+"F0.wireOp",EDGE,"E59")])],"isStart":false});
            var Q131;
            Q131=makeQuery(id+"F1.opExtrude","CAP_EDGE",EDGE,{"disambiguationData":[OSD([sQuery(id+"F0.wireOp",EDGE,"E55")])],"isStart":true});
            var Q132;
            Q132=makeQuery(id+"F1.opExtrude","CAP_EDGE",EDGE,{"disambiguationData":[OSD([sQuery(id+"F0.wireOp",EDGE,"E55")])],"isStart":false});
            var Q133;
            Q133=makeQuery(id+"F1.opExtrude","CAP_EDGE",EDGE,{"disambiguationData":[OSD([sQuery(id+"F0.wireOp",EDGE,"E88.trimOffspring")])],"isStart":true});
            var Q134;
            Q134=makeQuery(id+"F1.opExtrude","CAP_EDGE",EDGE,{"disambiguationData":[OSD([sQuery(id+"F0.wireOp",EDGE,"E3.0")])],"isStart":true});
            var Q135;
            Q135=makeQuery(id+"F1.opExtrude","CAP_EDGE",EDGE,{"disambiguationData":[OSD([sQuery(id+"F0.wireOp",EDGE,"E19")])],"isStart":true});
            fillet(context, id + "F2", {"entities" : qUnion([Q0, Q1, Q2, Q3, Q4, Q5, Q6, Q7, Q8, Q9, Q10, Q11, Q12, Q13, Q14, Q15, Q16, Q17, Q18, Q19, Q20, Q21, Q22, Q23, Q24, Q25, Q26, Q27, Q28, Q29, Q30, Q31, Q32, Q33, Q34, Q35, Q36, Q37, Q38, Q39, Q40, Q41, Q42, Q43, Q44, Q45, Q46, Q47, Q48, Q49, Q50, Q51, Q52, Q53, Q54, Q55, Q56, Q57, Q58, Q59, Q60, Q61, Q62, Q63, Q64, Q65, Q66, Q67, Q68, Q69, Q70, Q71, Q72, Q73, Q74, Q75, Q76, Q77, Q78, Q79, Q80, Q81, Q82, Q83, Q84, Q85, Q86, Q87, Q88, Q89, Q90, Q91, Q92, Q93, Q94, Q95, Q96, Q97, Q98, Q99, Q100, Q101, Q102, Q103, Q104, Q105, Q106, Q107, Q108, Q109, Q110, Q111, Q112, Q113, Q114, Q115, Q116, Q117, Q118, Q119, Q120, Q121, Q122, Q123, Q124, Q125, Q126, Q127, Q128, Q129, Q130, Q131, Q132, Q133, Q134, Q135]), "radius" : 0.4 * mm, "tangentPropagation" : true, "allowEdgeOverflow" : false});
        }
    });
